# Revit family: UNB_Adapto_U8415_BIM_DE
name_source: partatom
category: Plumbing Fixtures
revit_build: Autodesk Revit 2017 (Build: 20160225_1515(x64)
units: mm (PartAtom-declared; Revit-internal decimal feet)

## family parameters
Always vertical = No
Cut with Voids When Loaded = No
OmniClass Number = 23.45.05.14.21.11
OmniClass Title = Bath/Shower Units
Part Type = Normal
Room Calculation Point = No
Round Connector Dimension = Use Diameter
Shared = No
Work Plane-Based = No

## types (4) — shared parameters
Accessories = http://www.idealstandard.de
AreaUnits = Millimeter
AssetType = Fest
BIMobject category = Accessories
BIMobject category code = sanitary-accessories1
BIMobject main category = Sanitary
BIMobject main category code = sanitary
BOSUseNativeGeometries = 1
Brand = Ideal Standard
Brand url = http://www.idealstandard.co.uk
CodePerformance = FSC
ConnectionType = Mechanical
CurrencyUnit = €
CurrentRevision = 1
Date of publishing = 2018_04_13
DurationUnit = Jahr
Edition number = 1
IfcExportAs = IfcFurnitureType
IfcExportType = BATHROOM FURNITURE
Installation instructions = http://www.idealstandard.de
InstallationDate = 1900-12-31T23:59:59
InstallationInstructions = http://www.idealstandard.de
LinearUnits = Millimeter
MaintenanceInformation = http://www.idealstandard.de
Manufacturer name = Ideal Standard
ManufacturerURL = http://www.idealstandard.de
NBS Reference Code = 45-35-72/320
NBS Reference Description = Bathroom Integrated Ductwork
NettWeight = 4,00 KG
Nominal height = 12
Nominal width = 850
NominalDepth = 505 mm  [stored 1.65682 ft]
NominalHeight = 12 mm  [stored 0.0393701 ft]
NominalLength = 505 mm  [stored 1.65682 ft]
NominalWidth = 850 mm  [stored 2.78871 ft]
Product Guid = caf7ba2b-4c38-44fd-b527-241e74253be4
Product SKU = U8415
Product data url = https://bimobject.com
Product family = Sanitary
Product group = Bathroom Furniture
Product url = http://www.idealstandard.de
ProductInformation = http://www.idealstandard.de
QR code = http://bimobject.com
ReplacementCost = 0
Shape = Rechteckig
Size = 12 x 505 x 850mm
Space = intern
SpareParts = http://www.idealstandard.de
SustainabilityPerformance = FSC
Technical description = http://www.idealstandard.de
URL = http://www.idealstandard.de
Uniclass 2.0 Code = Pr_40_30_78_05
Uniclass 2.0 Description = Bathroom furniture
Uniclass 2015 Code = Pr_40_30_78_05
Uniclass 2015 Name = Bathroom furniture
Uniclass2015Code = Pr_40_30_78_05
Uniclass2015Title = Bathroom furniture
Uniclass2015Version = Products v1.1
Version = 1
VolumeUnits = Litres
WarrantyStartDate = 1900-12-31T23:59:59
zero-valued in all types: Cost, Weight Net (Kg)

## per-type parameters (varying)
| type | BIMObjectName | Color | Description | Features | Finish | MainColor | Model | ModelNumber | ModelReference | Name | Product name |
| U8415WG - W/TOP 85 | ISI_IdealStandard_BathroomFurniture_Adapto_U8415WG | White | W/TOP 85 | W/TOP 85 | White | White | U8415WG | U8415WG | W/TOP 85 | IdealStandard_BathroomFurniture_Adapto_U8415WG_ISI | W/TOP 85 |
| U8415FF - ADAPTO WORKTOP 85 WD LBRN | ISI_IdealStandard_BathroomFurniture_Adapto_U8415FF | Wood Light Brown | ADAPTO WORKTOP 85 WD LBRN | WORKTOP 85 WD LBRN | Wood Light Brown | Wood Light Brown | U8415FF | U8415FF | ADAPTO WORKTOP 85 WD LBRN | IdealStandard_BathroomFurniture_Adapto_U8415FF_ISI | ADAPTO WORKTOP 85 WD LBRN |
| U8415FW - ADAPTO WORKTOP 85 WD DARK | ISI_IdealStandard_BathroomFurniture_Adapto_U8415FW | Wood Dark Brown | ADAPTO WORKTOP 85 WD DARK | WORKTOP 85 WD DARK | Wood Dark Brown | Wood Dark Brown | U8415FW | U8415FW | ADAPTO WORKTOP 85 WD DARK | IdealStandard_BathroomFurniture_Adapto_U8415FW_ISI | ADAPTO WORKTOP 85 WD DARK |
| U8415FX - ADAPTO WORKTOP 85 GRY STN | ISI_IdealStandard_BathroomFurniture_Adapto_U8415FX | Grey | ADAPTO WORKTOP 85 GRY STN | WORKTOP 85 GRY STN | Grey | Grey | U8415FX | U8415FX | ADAPTO WORKTOP 85 GRY STN | IdealStandard_BathroomFurniture_Adapto_U8415FX_ISI | ADAPTO WORKTOP 85 GRY STN |

note: [stored X ft] marks values corroborated as IEEE doubles in the binary element streams (Revit-internal decimal feet)

## geometry (parser evidence)
native form markers: Sweep x3
no freeform markers — native parametric forms only
